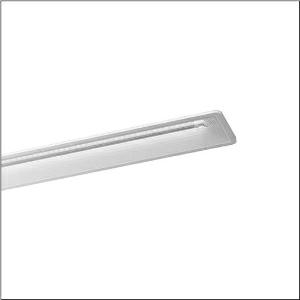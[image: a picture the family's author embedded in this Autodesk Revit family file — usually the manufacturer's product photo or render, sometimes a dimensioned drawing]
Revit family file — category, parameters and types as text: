
# Revit family: taris_r__21_5mt116704wd_f6c8
name_source: partatom
category: Lighting Fixtures
units: mm (PartAtom-declared; Revit-internal decimal feet)

## family parameters
Cut with Voids When Loaded = No
Host = Face
Light Source = No
Part Type = Normal
Room Calculation Point = No
Round Connector Dimension = Use Diameter
Shared = No

## types (1)
- Taris® 21 (1 x LED, 4910 lm, 30.6 W, 4000K)
    Apparent Load = 31 VA
    CIE Flux Codes = 73 96 99 100 100
    Color Rendering = 80
    Color Temperature = 4000K
    Default Elevation = 1800 mm
    Description = Taris® 21, office luminaire, primary anti-glare with micro louvre, primary optical cover: axial lens, of PMMA, structured, CAT 2 (L<= 1500cd/m²), light emission: direct distribution, primary light characteristic: symmetric, installation type: recessed, LED, rated luminous flux: 4.910lm, luminous efficacy: 160lm/W, light colour: 840, colour temperature: 4000K, control gear: ECG, with terminal, 5-pole, mains connection: 230V, AC, 50Hz, rated input power: 31W, housing, luminaire housing, of plastic, traffic white (RAL 9016), module: M625, length: 1.250mm, width: 150mm, height: 76mm, recess depth: 106mm, protection rating (complete): IP20, insulation class (complete): insulation class I (protective earthing), certification: CE, ENEC, VDE, protection symbol: F, impact resistance: IK02, permissible operating ambient temperature: 0..+35°C, standard: EN 50419, packaging unit: 1 piece
    Height = 0 mm  [stored 0 ft]
    Lamp = 1 x LED
    Lamp Light Flux = 4910 lm
    Lamp Power = 30.6 W
    Lamp count = 1
    Length = 1243 mm
    Luminous efficacy = 160 lm/W
    Manufacturer = Siteco
    ModVariant = No
    Model = 5MT116704WD
    Mounting Place = Ceiling
    Mounting Type = Recessed
    Number of Poles = 1
    OnlyDefault = Yes
    Power Factor = 1
    Product Name = Taris® 21
    Product group = office luminaire | ceiling recessed
    ProductGroupID = 401
    Protection Class = Protection class I
    Protection Degree = IP 20
    RLX_Detail_Level = 1
    RLX_Emergency_Light_Flux = 0 lm
    RLX_Emergency_Type = 0
    RLX_Emergency_Type_DB = No
    RlxData = <blob elided: 26109 chars, md5=b5ccf1ca>
    Socket = socket
    Standby Power = 0 W
    System Light Flux = 4910 lm
    System Power = 31 W
    Type Comments = Product without accessories
    Type Image = l_1004723.jpg
    URL = http://relux.com
    VarID = ---
    Voltage = 0 V
    Weight = 0.00 kg
    Width = 144 mm

note: [stored X ft] marks values corroborated as IEEE doubles in the binary element streams (Revit-internal decimal feet)

## geometry (parser evidence)
native form markers: Blend x4, Sweep x10
no freeform markers — native parametric forms only
